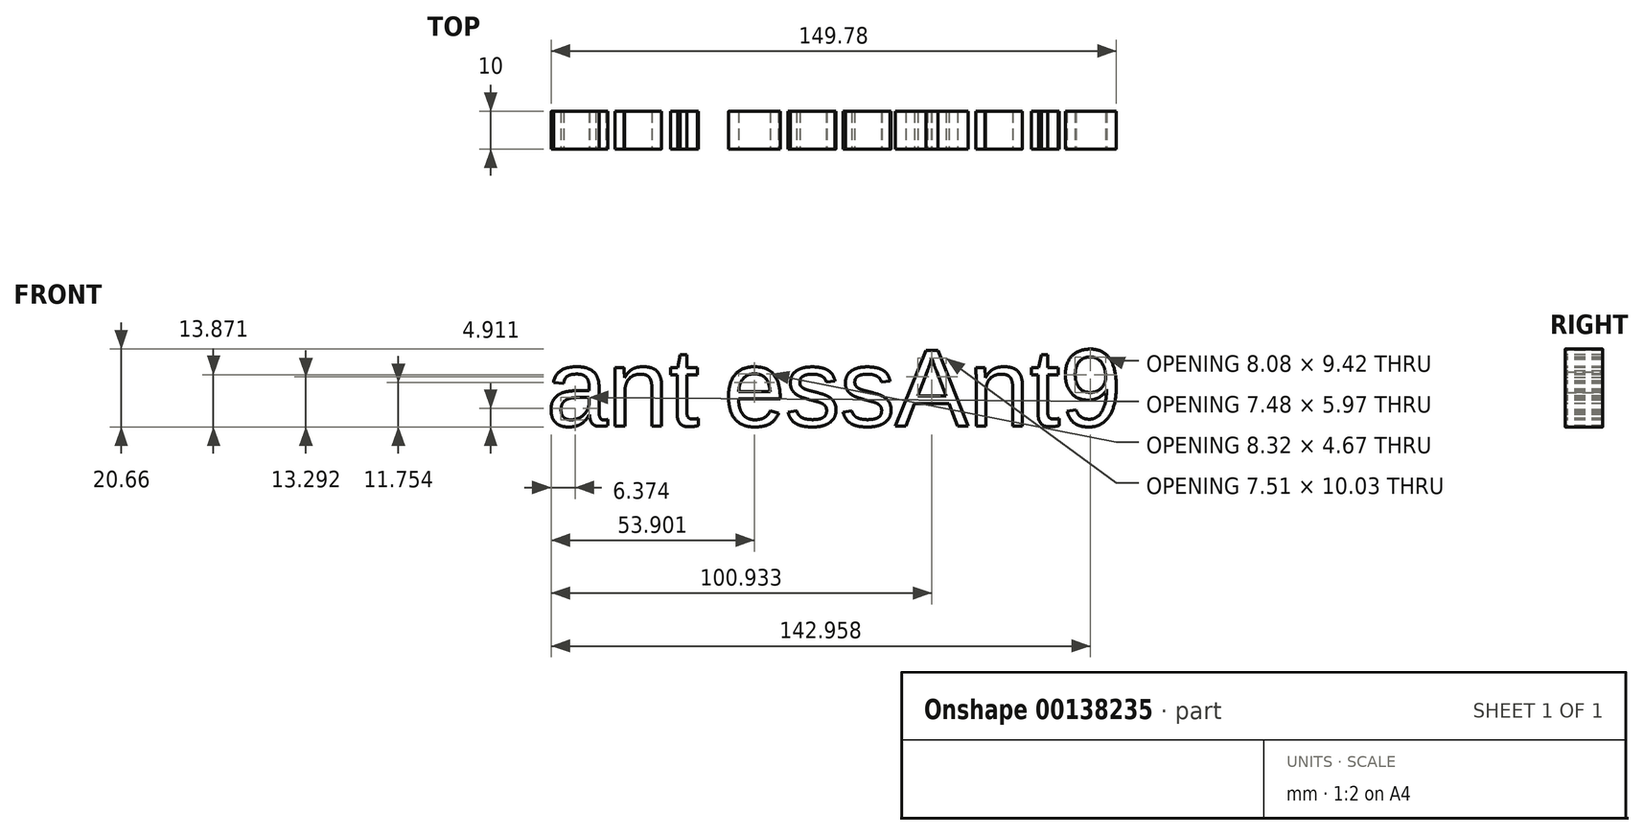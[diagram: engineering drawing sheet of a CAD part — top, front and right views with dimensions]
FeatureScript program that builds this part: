
annotation { "Feature Type Name" : "Feature", "Feature Type Description" : "" }
export const myFeature = defineFeature(function(context is Context, id is Id, definition is map)
    precondition{}
    {
        {
            var Q0;
            Q0=qCreatedBy(makeId("Front.planeOp"),FACE);
            var sketch = newSketch(context, id + "F0", { "sketchPlane" : qUnion([Q0])});
            skLineSegment(sketch, "E0", {"start": v(0, 10) * mm, "end": v(-90, 10) * mm});
            skLineSegment(sketch, "E1", {"start": v(0, 10) * mm, "end": v(90.58, 10) * mm});
            skLineSegment(sketch, "E2", {"start": v(-90, 10) * mm, "end": v(-90, 31) * mm});
            skLineSegment(sketch, "E3", {"start": v(90.58, 10) * mm, "end": v(90.58, 31) * mm});
            skLineSegment(sketch, "E4", {"start": v(-90, 31) * mm, "end": v(90.58, 31) * mm});
            skText(sketch, "E5", { "text": "WantlessAnt9", "fontName": "Arimo-Regular.ttf"});
            const initialGuessF0  = {"E5": [-0.09, 0.01, 1, 0, 0.021]};
            skSetInitialGuess(sketch, initialGuessF0);
            skSolve(sketch);
        }
        {
            var Q0;
            {var subQ6=sQuery(id+"F0.wireOp",EDGE,"E5.sketch_text.stroke-230");Q0=makeQuery(id+"F0.imprint","IMPRINT",FACE,{"disambiguationData":[TD([[makeQuery(id+"F0.imprint","IMPRINT",EDGE,{"derivedFrom":subQ6}),-1.0]])]});}
            var Q1;
            {var subQ0=sQuery(id+"F0.wireOp",EDGE,"E5.sketch_text.stroke-232");var subQ1=sQuery(id+"F0.wireOp",EDGE,"E1");var subQ2=makeQuery(id+"F0.imprint","INTERSECT",VERTEX,{"derivedFrom":[subQ1,subQ0]});Q1=makeQuery(id+"F0.imprint","IMPRINT",FACE,{"disambiguationData":[TD([[makeQuery(id+"F0.imprint","IMPRINT",EDGE,{"disambiguationData":[TD([[subQ2,-1.0]])],"derivedFrom":subQ1}),-1.0]])]});}
            var Q2;
            {var subQ0=sQuery(id+"F0.wireOp",EDGE,"E5.sketch_text.stroke-214");var subQ1=sQuery(id+"F0.wireOp",EDGE,"E1");var subQ2=makeQuery(id+"F0.imprint","INTERSECT",VERTEX,{"derivedFrom":[subQ1,subQ0]});Q2=makeQuery(id+"F0.imprint","IMPRINT",FACE,{"disambiguationData":[TD([[makeQuery(id+"F0.imprint","IMPRINT",EDGE,{"disambiguationData":[TD([[subQ2,-1.0]])],"derivedFrom":subQ1}),-1.0]])]});}
            var Q3;
            {var subQ6=sQuery(id+"F0.wireOp",EDGE,"E5.sketch_text.stroke-215");Q3=makeQuery(id+"F0.imprint","IMPRINT",FACE,{"disambiguationData":[TD([[makeQuery(id+"F0.imprint","IMPRINT",EDGE,{"derivedFrom":subQ6}),-1.0]])]});}
            var Q4;
            Q4=makeQuery(id+"F0.imprint","IMPRINT",FACE,{"disambiguationData":[TD([[makeQuery(id+"F0.imprint","IMPRINT",EDGE,{"derivedFrom":sQuery(id+"F0.wireOp",EDGE,"E5.sketch_text.stroke-192")}),-1.0]])]});
            var Q5;
            Q5=makeQuery(id+"F0.imprint","IMPRINT",FACE,{"disambiguationData":[TD([[makeQuery(id+"F0.imprint","IMPRINT",EDGE,{"derivedFrom":sQuery(id+"F0.wireOp",EDGE,"E5.sketch_text.stroke-177")}),-1.0]])]});
            var Q6;
            {var subQ6=sQuery(id+"F0.wireOp",EDGE,"E5.sketch_text.stroke-146");Q6=makeQuery(id+"F0.imprint","IMPRINT",FACE,{"disambiguationData":[TD([[makeQuery(id+"F0.imprint","IMPRINT",EDGE,{"derivedFrom":subQ6}),-1.0]])]});}
            var Q7;
            {var subQ2=sQuery(id+"F0.wireOp",EDGE,"E5.sketch_text.stroke-115");Q7=makeQuery(id+"F0.imprint","IMPRINT",FACE,{"disambiguationData":[TD([[makeQuery(id+"F0.imprint","IMPRINT",EDGE,{"derivedFrom":subQ2}),-1.0]])]});}
            var Q8;
            {var subQ0=sQuery(id+"F0.wireOp",EDGE,"E5.sketch_text.stroke-148");var subQ1=sQuery(id+"F0.wireOp",EDGE,"E1");var subQ2=makeQuery(id+"F0.imprint","INTERSECT",VERTEX,{"derivedFrom":[subQ1,subQ0]});Q8=makeQuery(id+"F0.imprint","IMPRINT",FACE,{"disambiguationData":[TD([[makeQuery(id+"F0.imprint","IMPRINT",EDGE,{"disambiguationData":[TD([[subQ2,-1.0]])],"derivedFrom":subQ1}),-1.0]])]});}
            var Q9;
            {var subQ0=sQuery(id+"F0.wireOp",EDGE,"E5.sketch_text.stroke-117");var subQ1=sQuery(id+"F0.wireOp",EDGE,"E1");var subQ2=makeQuery(id+"F0.imprint","INTERSECT",VERTEX,{"derivedFrom":[subQ1,subQ0]});Q9=makeQuery(id+"F0.imprint","IMPRINT",FACE,{"disambiguationData":[TD([[makeQuery(id+"F0.imprint","IMPRINT",EDGE,{"disambiguationData":[TD([[subQ2,-1.0]])],"derivedFrom":subQ1}),-1.0]])]});}
            var Q10;
            {var subQ0=sQuery(id+"F0.wireOp",EDGE,"E5.sketch_text.stroke-102");var subQ1=sQuery(id+"F0.wireOp",EDGE,"E0");var subQ2=makeQuery(id+"F0.imprint","INTERSECT",VERTEX,{"derivedFrom":[subQ1,subQ0]});Q10=makeQuery(id+"F0.imprint","IMPRINT",FACE,{"disambiguationData":[TD([[makeQuery(id+"F0.imprint","IMPRINT",EDGE,{"disambiguationData":[TD([[subQ2,-1.0]])],"derivedFrom":subQ1}),1.0]])]});}
            var Q11;
            Q11=makeQuery(id+"F0.imprint","IMPRINT",FACE,{"disambiguationData":[TD([[makeQuery(id+"F0.imprint","IMPRINT",EDGE,{"derivedFrom":sQuery(id+"F0.wireOp",EDGE,"E5.sketch_text.stroke-97")}),-1.0]])]});
            var Q12;
            {var subQ5=sQuery(id+"F0.wireOp",EDGE,"E5.sketch_text.stroke-96");Q12=makeQuery(id+"F0.imprint","IMPRINT",FACE,{"disambiguationData":[TD([[makeQuery(id+"F0.imprint","IMPRINT",EDGE,{"derivedFrom":subQ5}),-1.0]])]});}
            var Q13;
            {var subQ0=sQuery(id+"F0.wireOp",EDGE,"E5.sketch_text.stroke-78");Q13=makeQuery(id+"F0.imprint","IMPRINT",FACE,{"disambiguationData":[TD([[makeQuery(id+"F0.imprint","IMPRINT",EDGE,{"derivedFrom":subQ0}),-1.0]])]});}
            var Q14;
            {var subQ0=sQuery(id+"F0.wireOp",EDGE,"E5.sketch_text.stroke-76");var subQ1=sQuery(id+"F0.wireOp",EDGE,"E0");var subQ2=makeQuery(id+"F0.imprint","INTERSECT",VERTEX,{"derivedFrom":[subQ1,subQ0]});Q14=makeQuery(id+"F0.imprint","IMPRINT",FACE,{"disambiguationData":[TD([[makeQuery(id+"F0.imprint","IMPRINT",EDGE,{"disambiguationData":[TD([[subQ2,-1.0]])],"derivedFrom":subQ1}),1.0]])]});}
            var Q15;
            Q15=makeQuery(id+"F0.imprint","IMPRINT",FACE,{"disambiguationData":[TD([[makeQuery(id+"F0.imprint","IMPRINT",EDGE,{"derivedFrom":sQuery(id+"F0.wireOp",EDGE,"E5.sketch_text.stroke-55")}),-1.0]])]});
            var Q16;
            {var subQ6=sQuery(id+"F0.wireOp",EDGE,"E5.sketch_text.stroke-21");Q16=makeQuery(id+"F0.imprint","IMPRINT",FACE,{"disambiguationData":[TD([[makeQuery(id+"F0.imprint","IMPRINT",EDGE,{"derivedFrom":subQ6}),-1.0]])]});}
            var Q17;
            {var subQ0=sQuery(id+"F0.wireOp",EDGE,"E5.sketch_text.stroke-44");var subQ1=sQuery(id+"F0.wireOp",EDGE,"E0");var subQ2=makeQuery(id+"F0.imprint","INTERSECT",VERTEX,{"derivedFrom":[subQ1,subQ0]});Q17=makeQuery(id+"F0.imprint","IMPRINT",FACE,{"disambiguationData":[TD([[makeQuery(id+"F0.imprint","IMPRINT",EDGE,{"disambiguationData":[TD([[subQ2,-1.0]])],"derivedFrom":subQ1}),1.0]])]});}
            var Q18;
            Q18=makeQuery(id+"F0.imprint","IMPRINT",FACE,{"disambiguationData":[TD([[makeQuery(id+"F0.imprint","IMPRINT",EDGE,{"derivedFrom":sQuery(id+"F0.wireOp",EDGE,"E5.sketch_text.stroke-0")}),-1.0]])]});
            extrude(context, id + "F1", {"entities" : qUnion([Q0, Q1, Q2, Q3, Q4, Q5, Q6, Q7, Q8, Q9, Q10, Q11, Q12, Q13, Q14, Q15, Q16, Q17, Q18]), "oppositeDirection" : true, "depth" : 10 * mm});
        }
    });
